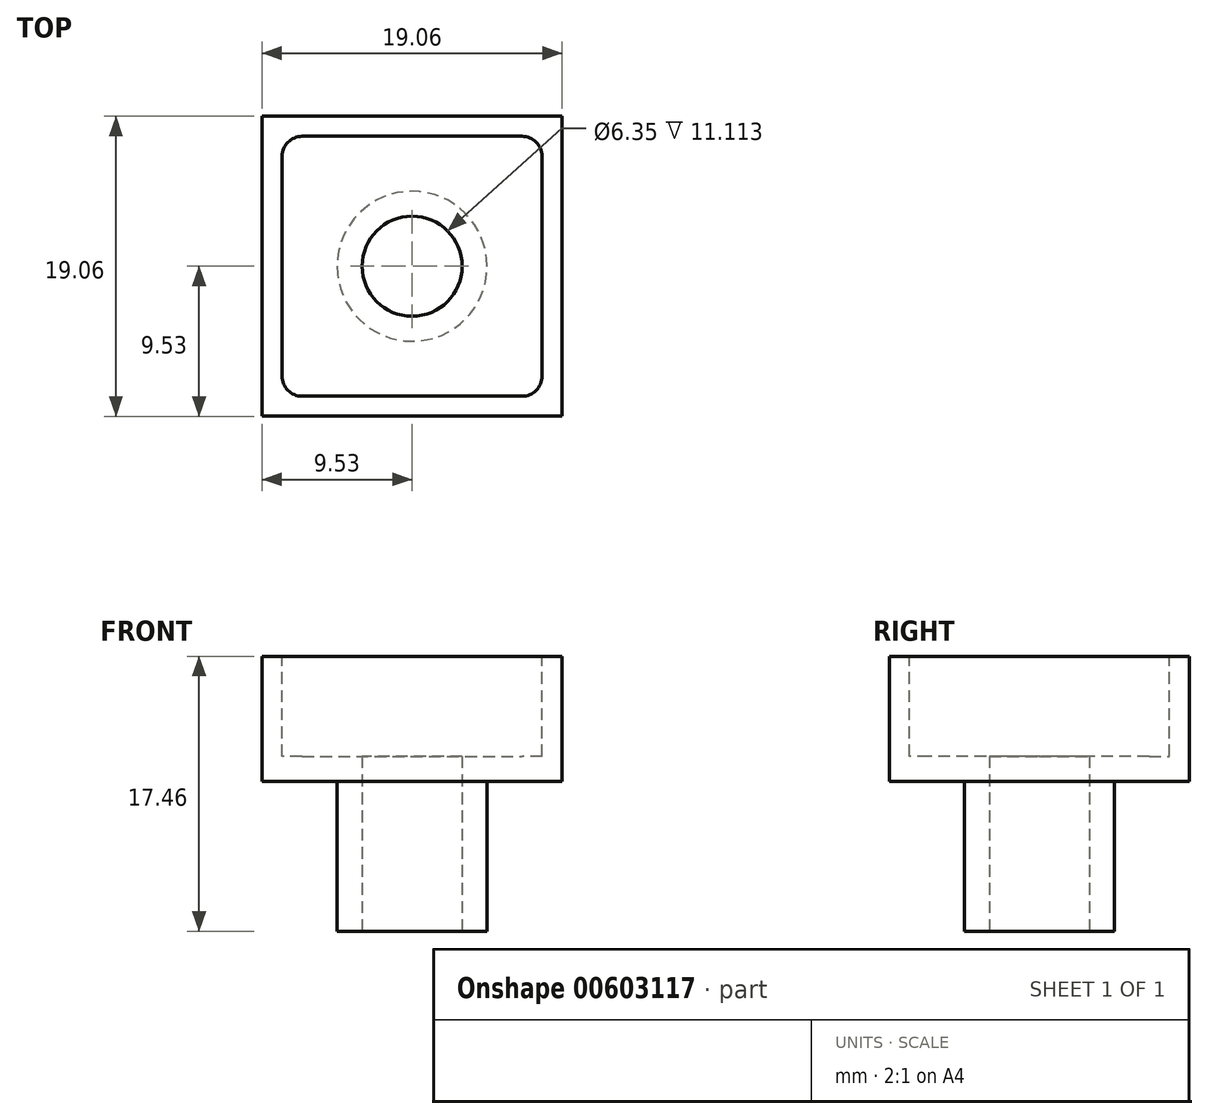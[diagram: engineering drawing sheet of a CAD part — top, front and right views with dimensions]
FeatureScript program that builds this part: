
annotation { "Feature Type Name" : "Feature", "Feature Type Description" : "" }
export const myFeature = defineFeature(function(context is Context, id is Id, definition is map)
    precondition{}
    {
        {
            var Q0;
            Q0=qCreatedBy(makeId("Top.planeOp"),FACE);
            var sketch = newSketch(context, id + "F0", { "sketchPlane" : qUnion([Q0])});
            skCircle(sketch, "E0", {"center": v(0, 0) * mm, "radius": 4.76 * mm});
            skSolve(sketch);
        }
        {
            var Q0;
            Q0=qSketchRegion(id+"F0",true);
            extrude(context, id + "F1", {"entities" : qUnion([Q0]), "depth" : 17.46 * mm});
        }
        {
            var Q0;
            Q0=makeQuery(id+"F0.imprint","IMPRINT",FACE,{"disambiguationData":[TD([[makeQuery(id+"F0.imprint","IMPRINT",EDGE,{"derivedFrom":sQuery(id+"F0.wireOp",EDGE,"E0")}),1.0]])]});
            var sketch = newSketch(context, id + "F2", { "sketchPlane" : qUnion([Q0])});
            skCircle(sketch, "E1", {"center": v(0, 0) * mm, "radius": 3.18 * mm});
            skSolve(sketch);
        }
        {
            var Q0;
            Q0=qCreatedBy(makeId("Front.planeOp"),FACE);
            var sketch = newSketch(context, id + "F3", { "sketchPlane" : qUnion([Q0])});
            skLineSegment(sketch, "E2", {"start": v(0, 0) * mm, "end": v(0, 17.46) * mm, "construction": true});
            skLineSegment(sketch, "E3", {"start": v(0, 0) * mm, "end": v(-9.53, 0) * mm, "construction": true});
            skLineSegment(sketch, "E4.bottom", {"start": v(-9.52, 17.46) * mm, "end": v(9.52, 17.46) * mm});
            skLineSegment(sketch, "E4.top", {"start": v(-9.53, 9.53) * mm, "end": v(9.52, 9.53) * mm});
            skLineSegment(sketch, "E4.left", {"start": v(-9.53, 17.46) * mm, "end": v(-9.53, 9.53) * mm});
            skLineSegment(sketch, "E4.right", {"start": v(9.52, 17.46) * mm, "end": v(9.52, 9.53) * mm});
            skSolve(sketch);
        }
        {
            var Q0;
            Q0=qSketchRegion(id+"F3",true);
            extrude(context, id + "F4", {"entities" : qUnion([Q0]), "operationType" : NewBodyOperationType.ADD, "endBound" : BoundingType.SYMMETRIC, "depth" : 19.05 * mm});
        }
        {
            var Q0;
            Q0=makeQuery(id+"F4.boolean.opBoolean","MERGE",FACE,{"derivedFrom":[makeQuery(id+"F1.opExtrude","CAP_FACE",FACE,{"disambiguationData":[OSD([sQuery(id+"F0.wireOp",EDGE,"E0")])],"isStart":false}),makeQuery(id+"F4.opExtrude","SWEPT_FACE",FACE,{"disambiguationData":[OSD([sQuery(id+"F3.wireOp",EDGE,"E4.bottom")])]})]});
            var sketch = newSketch(context, id + "F5", { "sketchPlane" : qUnion([Q0])});
            skLineSegment(sketch, "E5.bottom", {"start": v(-6.98, 8.26) * mm, "end": v(6.99, 8.26) * mm});
            skLineSegment(sketch, "E5.top", {"start": v(-6.98, -8.26) * mm, "end": v(6.99, -8.26) * mm});
            skLineSegment(sketch, "E5.left", {"start": v(-8.25, 6.99) * mm, "end": v(-8.25, -6.99) * mm});
            skLineSegment(sketch, "E5.right", {"start": v(8.26, 6.99) * mm, "end": v(8.26, -6.99) * mm});
            skPoint(sketch, "E6.visualSharp", {"position": v(-8.25, 8.26) * mm});
            skArc(sketch, "E6.filletArc", {"start": v(-6.98, 8.26) * mm, "mid": v(-7.88, 7.88) * mm, "end": v(-8.25, 6.99) * mm});
            skPoint(sketch, "E7.visualSharp", {"position": v(8.26, 8.26) * mm});
            skArc(sketch, "E7.filletArc", {"start": v(8.26, 6.99) * mm, "mid": v(7.88, 7.88) * mm, "end": v(6.99, 8.26) * mm});
            skPoint(sketch, "E8.visualSharp", {"position": v(8.26, -8.26) * mm});
            skArc(sketch, "E8.filletArc", {"start": v(6.99, -8.26) * mm, "mid": v(7.88, -7.88) * mm, "end": v(8.26, -6.99) * mm});
            skPoint(sketch, "E9.visualSharp", {"position": v(-8.25, -8.26) * mm});
            skArc(sketch, "E9.filletArc", {"start": v(-8.25, -6.99) * mm, "mid": v(-7.88, -7.88) * mm, "end": v(-6.98, -8.26) * mm});
            skSolve(sketch);
        }
        {
            var Q0;
            Q0=qSketchRegion(id+"F5",true);
            extrude(context, id + "F6", {"entities" : qUnion([Q0]), "operationType" : NewBodyOperationType.REMOVE, "oppositeDirection" : true, "depth" : 6.35 * mm});
        }
        {
            var Q0;
            Q0=qSketchRegion(id+"F2",true);
            extrude(context, id + "F7", {"entities" : qUnion([Q0]), "operationType" : NewBodyOperationType.REMOVE, "depth" : 17.46 * mm});
        }
    });
